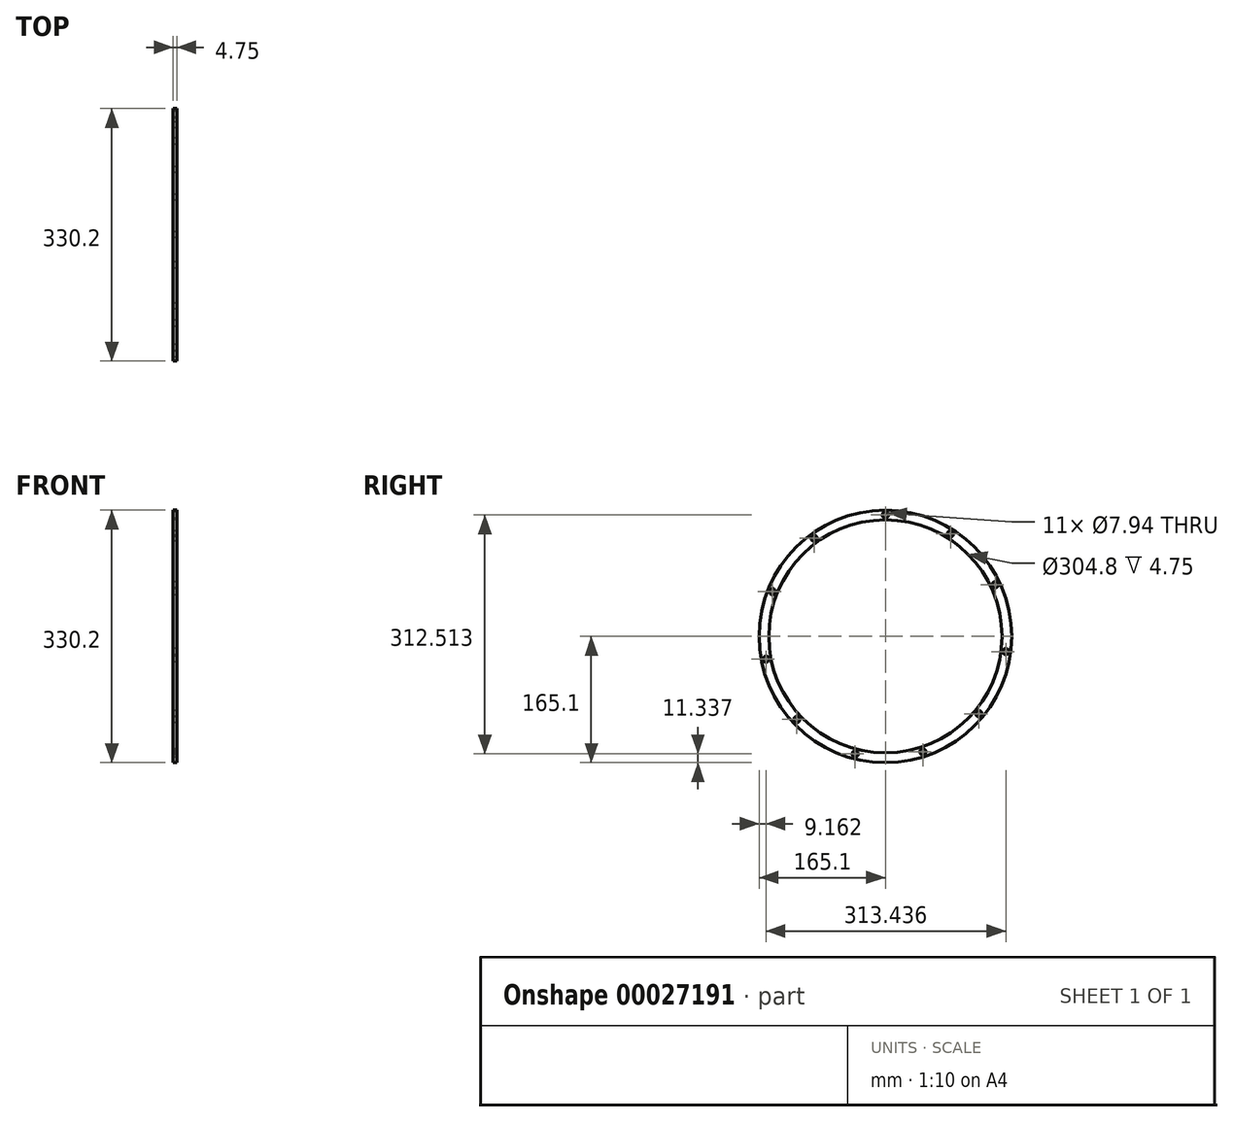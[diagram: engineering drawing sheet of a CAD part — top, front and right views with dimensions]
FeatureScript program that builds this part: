
annotation { "Feature Type Name" : "Feature", "Feature Type Description" : "" }
export const myFeature = defineFeature(function(context is Context, id is Id, definition is map)
    precondition{}
    {
        {
            var Q0;
            Q0=qCreatedBy(makeId("Right.planeOp"),FACE);
            var sketch = newSketch(context, id + "F0", { "sketchPlane" : qUnion([Q0])});
            skCircle(sketch, "E0", {"center": v(0, 0) * mm, "radius": 165.1 * mm});
            skCircle(sketch, "E1", {"center": v(0, 0) * mm, "radius": 152.4 * mm});
            skPoint(sketch, "E2", {"position": v(0, 152.4) * mm});
            skPoint(sketch, "E3", {"position": v(0, 165.1) * mm});
            skLineSegment(sketch, "E4", {"start": v(0, 165.1) * mm, "end": v(0, 152.4) * mm});
            skPoint(sketch, "E5", {"position": v(0, 158.75) * mm});
            skCircle(sketch, "E6", {"center": v(0, 158.75) * mm, "radius": 3.97 * mm});
            skCircle(sketch, "E7.1.0", {"center": v(85.06, 134.04) * mm, "radius": 3.97 * mm});
            skCircle(sketch, "E7.2.0", {"center": v(143.64, 67.6) * mm, "radius": 3.97 * mm});
            skLineSegment(sketch, "E7.anchor1", {"start": v(0, 0) * mm, "end": v(0, 158.75) * mm, "construction": true});
            skLineSegment(sketch, "E7.anchor2", {"start": v(0, 0) * mm, "end": v(-93.31, 128.43) * mm, "construction": true});
            skCircle(sketch, "E8.1.3.0", {"center": v(157.5, -19.9) * mm, "radius": 3.97 * mm});
            skCircle(sketch, "E8.1.4.0", {"center": v(122.32, -101.2) * mm, "radius": 3.97 * mm});
            skCircle(sketch, "E8.1.5.0", {"center": v(49.06, -150.98) * mm, "radius": 3.97 * mm});
            skCircle(sketch, "E8.1.6.0", {"center": v(-39.48, -153.76) * mm, "radius": 3.97 * mm});
            skCircle(sketch, "E8.1.7.0", {"center": v(-115.72, -108.67) * mm, "radius": 3.97 * mm});
            skCircle(sketch, "E8.1.8.0", {"center": v(-155.94, -29.75) * mm, "radius": 3.97 * mm});
            skCircle(sketch, "E8.1.9.0", {"center": v(-147.6, 58.44) * mm, "radius": 3.97 * mm});
            skCircle(sketch, "E9.1.10.0", {"center": v(-93.31, 128.43) * mm, "radius": 3.97 * mm});
            skSolve(sketch);
        }
        {
            var Q0;
            Q0 = qSketchRegion(id + "F0", true);
            extrude(context, id + "F1", {"entities" : qUnion([Q0]), "depth" : 4.75 * mm});
        }
    });
